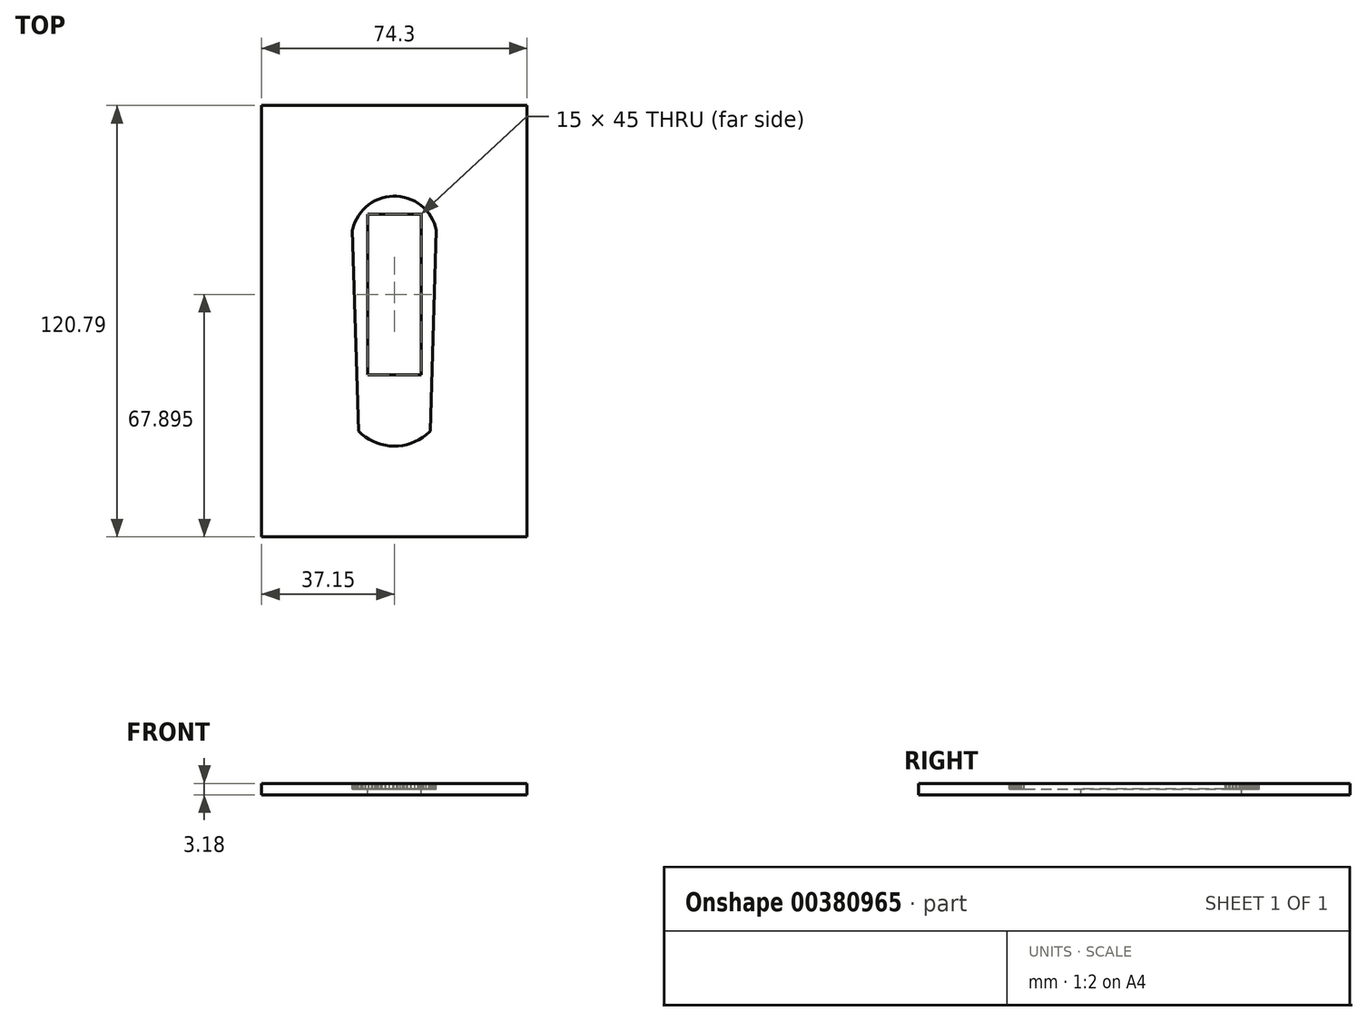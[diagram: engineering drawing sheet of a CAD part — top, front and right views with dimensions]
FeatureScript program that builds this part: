
annotation { "Feature Type Name" : "Feature", "Feature Type Description" : "" }
export const myFeature = defineFeature(function(context is Context, id is Id, definition is map)
    precondition{}
    {
        {
            var Q0;
            Q0=qCreatedBy(makeId("Top.planeOp"),FACE);
            var sketch = newSketch(context, id + "F0", { "sketchPlane" : qUnion([Q0])});
            skLineSegment(sketch, "E0", {"start": v(-11.75, 70.44) * mm, "end": v(-10, 14.2) * mm});
            skLineSegment(sketch, "E1", {"start": v(10, 14.2) * mm, "end": v(11.75, 70.44) * mm});
            skCircle(sketch, "E2", {"center": v(0, 64) * mm, "radius": 1.12 * mm, "construction": true});
            skCircle(sketch, "E3", {"center": v(0, 12.42) * mm, "radius": 1.12 * mm, "construction": true});
            skLineSegment(sketch, "E4", {"start": v(11.75, 70.44) * mm, "end": v(11.5, 71.45) * mm});
            skLineSegment(sketch, "E5", {"start": v(11.5, 71.45) * mm, "end": v(11.15, 72.44) * mm});
            skLineSegment(sketch, "E6", {"start": v(11.15, 72.44) * mm, "end": v(10.72, 73.4) * mm});
            skLineSegment(sketch, "E7", {"start": v(10.72, 73.4) * mm, "end": v(10.2, 74.3) * mm});
            skLineSegment(sketch, "E8", {"start": v(10.2, 74.3) * mm, "end": v(9.62, 75.17) * mm});
            skLineSegment(sketch, "E9", {"start": v(9.62, 75.17) * mm, "end": v(8.96, 75.99) * mm});
            skLineSegment(sketch, "E10", {"start": v(8.96, 75.99) * mm, "end": v(8.23, 76.74) * mm});
            skLineSegment(sketch, "E11", {"start": v(8.23, 76.74) * mm, "end": v(7.43, 77.42) * mm});
            skLineSegment(sketch, "E12", {"start": v(7.43, 77.42) * mm, "end": v(6.59, 78.03) * mm});
            skLineSegment(sketch, "E13", {"start": v(6.59, 78.03) * mm, "end": v(5.69, 78.57) * mm});
            skLineSegment(sketch, "E14", {"start": v(5.69, 78.57) * mm, "end": v(4.74, 79.02) * mm});
            skLineSegment(sketch, "E15", {"start": v(4.74, 79.02) * mm, "end": v(3.76, 79.4) * mm});
            skLineSegment(sketch, "E16", {"start": v(3.76, 79.4) * mm, "end": v(2.76, 79.68) * mm});
            skLineSegment(sketch, "E17", {"start": v(2.76, 79.68) * mm, "end": v(1.73, 79.87) * mm});
            skLineSegment(sketch, "E18", {"start": v(1.73, 79.87) * mm, "end": v(0.69, 79.98) * mm});
            skLineSegment(sketch, "E19", {"start": v(0.69, 79.98) * mm, "end": v(-0.36, 80) * mm});
            skLineSegment(sketch, "E20", {"start": v(-0.36, 80) * mm, "end": v(-1.4, 79.92) * mm});
            skLineSegment(sketch, "E21", {"start": v(-1.4, 79.92) * mm, "end": v(-2.44, 79.75) * mm});
            skLineSegment(sketch, "E22", {"start": v(-2.44, 79.75) * mm, "end": v(-3.45, 79.5) * mm});
            skLineSegment(sketch, "E23", {"start": v(-3.45, 79.5) * mm, "end": v(-4.44, 79.15) * mm});
            skLineSegment(sketch, "E24", {"start": v(-4.44, 79.15) * mm, "end": v(-5.4, 78.72) * mm});
            skLineSegment(sketch, "E25", {"start": v(-5.4, 78.72) * mm, "end": v(-6.3, 78.2) * mm});
            skLineSegment(sketch, "E26", {"start": v(-6.3, 78.2) * mm, "end": v(-7.17, 77.62) * mm});
            skLineSegment(sketch, "E27", {"start": v(-7.17, 77.62) * mm, "end": v(-7.99, 76.96) * mm});
            skLineSegment(sketch, "E28", {"start": v(-7.99, 76.96) * mm, "end": v(-8.74, 76.23) * mm});
            skLineSegment(sketch, "E29", {"start": v(-8.74, 76.23) * mm, "end": v(-9.42, 75.43) * mm});
            skLineSegment(sketch, "E30", {"start": v(-9.42, 75.43) * mm, "end": v(-10.03, 74.59) * mm});
            skLineSegment(sketch, "E31", {"start": v(-10.03, 74.59) * mm, "end": v(-10.57, 73.69) * mm});
            skLineSegment(sketch, "E32", {"start": v(-10.57, 73.69) * mm, "end": v(-11.02, 72.74) * mm});
            skLineSegment(sketch, "E33", {"start": v(-11.02, 72.74) * mm, "end": v(-11.4, 71.76) * mm});
            skLineSegment(sketch, "E34", {"start": v(-11.4, 71.76) * mm, "end": v(-11.68, 70.76) * mm});
            skLineSegment(sketch, "E35", {"start": v(-11.68, 70.76) * mm, "end": v(-11.75, 70.44) * mm});
            skLineSegment(sketch, "E36", {"start": v(-10, 14.2) * mm, "end": v(-9.1, 13.37) * mm});
            skLineSegment(sketch, "E37", {"start": v(-9.1, 13.37) * mm, "end": v(-8.15, 12.61) * mm});
            skLineSegment(sketch, "E38", {"start": v(-8.15, 12.61) * mm, "end": v(-7.12, 11.95) * mm});
            skLineSegment(sketch, "E39", {"start": v(-7.12, 11.95) * mm, "end": v(-6.05, 11.37) * mm});
            skLineSegment(sketch, "E40", {"start": v(-6.05, 11.37) * mm, "end": v(-4.92, 10.9) * mm});
            skLineSegment(sketch, "E41", {"start": v(-4.92, 10.9) * mm, "end": v(-3.76, 10.51) * mm});
            skLineSegment(sketch, "E42", {"start": v(-3.76, 10.51) * mm, "end": v(-2.57, 10.24) * mm});
            skLineSegment(sketch, "E43", {"start": v(-2.57, 10.24) * mm, "end": v(-1.36, 10.07) * mm});
            skLineSegment(sketch, "E44", {"start": v(-1.36, 10.07) * mm, "end": v(-0.14, 10) * mm});
            skLineSegment(sketch, "E45", {"start": v(-0.14, 10) * mm, "end": v(1.08, 10.04) * mm});
            skLineSegment(sketch, "E46", {"start": v(1.08, 10.04) * mm, "end": v(2.3, 10.19) * mm});
            skLineSegment(sketch, "E47", {"start": v(2.3, 10.19) * mm, "end": v(3.49, 10.44) * mm});
            skLineSegment(sketch, "E48", {"start": v(3.49, 10.44) * mm, "end": v(4.65, 10.8) * mm});
            skLineSegment(sketch, "E49", {"start": v(4.65, 10.8) * mm, "end": v(5.79, 11.25) * mm});
            skLineSegment(sketch, "E50", {"start": v(5.79, 11.25) * mm, "end": v(6.88, 11.8) * mm});
            skLineSegment(sketch, "E51", {"start": v(6.88, 11.8) * mm, "end": v(7.91, 12.45) * mm});
            skLineSegment(sketch, "E52", {"start": v(7.91, 12.45) * mm, "end": v(8.89, 13.18) * mm});
            skLineSegment(sketch, "E53", {"start": v(8.89, 13.18) * mm, "end": v(9.8, 14) * mm});
            skLineSegment(sketch, "E54", {"start": v(9.8, 14) * mm, "end": v(10, 14.2) * mm});
            skCircle(sketch, "E55", {"center": v(-0.85, 17.78) * mm, "radius": 0.45 * mm, "construction": true});
            skCircle(sketch, "E56", {"center": v(0.85, 17.78) * mm, "radius": 0.35 * mm, "construction": true});
            skCircle(sketch, "E57", {"center": v(2.84, 26.11) * mm, "radius": 0.5 * mm, "construction": true});
            skCircle(sketch, "E58", {"center": v(1.83, 31.2) * mm, "radius": 0.5 * mm, "construction": true});
            skCircle(sketch, "E59", {"center": v(3.86, 31.2) * mm, "radius": 0.5 * mm, "construction": true});
            skSolve(sketch);
        }
        {
            var Q0;
            Q0=qCreatedBy(makeId("Top.planeOp"),FACE);
            var sketch = newSketch(context, id + "F1", { "sketchPlane" : qUnion([Q0])});
            skLineSegment(sketch, "E60.bottom", {"start": v(-11.75, 80) * mm, "end": v(11.75, 80) * mm, "construction": true});
            skLineSegment(sketch, "E60.top", {"start": v(-11.75, 10) * mm, "end": v(11.75, 10) * mm, "construction": true});
            skLineSegment(sketch, "E60.left", {"start": v(-11.75, 80) * mm, "end": v(-11.75, 10) * mm, "construction": true});
            skLineSegment(sketch, "E60.right", {"start": v(11.75, 80) * mm, "end": v(11.75, 10) * mm, "construction": true});
            skLineSegment(sketch, "E61.0", {"start": v(-37.15, 105.4) * mm, "end": v(-37.15, -15.4) * mm});
            skLineSegment(sketch, "E61.1", {"start": v(-37.15, 105.4) * mm, "end": v(37.15, 105.4) * mm});
            skLineSegment(sketch, "E61.2", {"start": v(37.15, 105.4) * mm, "end": v(37.15, -15.4) * mm});
            skLineSegment(sketch, "E61.3", {"start": v(-37.15, -15.4) * mm, "end": v(37.15, -15.4) * mm});
            skSolve(sketch);
        }
        {
            var Q0;
            Q0 = qSketchRegion(id + "F1", true);
            extrude(context, id + "F2", {"entities" : qUnion([Q0]), "oppositeDirection" : true, "depth" : 3.17 * mm});
        }
        {
            var Q0;
            Q0 = qSketchRegion(id + "F0", true);
            extrude(context, id + "F3", {"entities" : qUnion([Q0]), "operationType" : NewBodyOperationType.REMOVE, "oppositeDirection" : true, "depth" : 1.57 * mm});
        }
        {
            var Q0;
            Q0=makeQuery(id+"F3.boolean.opBoolean","COPY",FACE,{"derivedFrom":makeQuery(id+"F3.opExtrude","CAP_FACE",FACE,{"disambiguationData":[OSD([sQuery(id+"F0.wireOp",EDGE,"E0"),sQuery(id+"F0.wireOp",EDGE,"E1"),sQuery(id+"F0.wireOp",EDGE,"E4"),sQuery(id+"F0.wireOp",EDGE,"E5"),sQuery(id+"F0.wireOp",EDGE,"E6"),sQuery(id+"F0.wireOp",EDGE,"E7"),sQuery(id+"F0.wireOp",EDGE,"E8"),sQuery(id+"F0.wireOp",EDGE,"E9"),sQuery(id+"F0.wireOp",EDGE,"E10"),sQuery(id+"F0.wireOp",EDGE,"E11"),sQuery(id+"F0.wireOp",EDGE,"E12"),sQuery(id+"F0.wireOp",EDGE,"E13"),sQuery(id+"F0.wireOp",EDGE,"E14"),sQuery(id+"F0.wireOp",EDGE,"E15"),sQuery(id+"F0.wireOp",EDGE,"E16"),sQuery(id+"F0.wireOp",EDGE,"E17"),sQuery(id+"F0.wireOp",EDGE,"E18"),sQuery(id+"F0.wireOp",EDGE,"E19"),sQuery(id+"F0.wireOp",EDGE,"E20"),sQuery(id+"F0.wireOp",EDGE,"E21"),sQuery(id+"F0.wireOp",EDGE,"E22"),sQuery(id+"F0.wireOp",EDGE,"E23"),sQuery(id+"F0.wireOp",EDGE,"E24"),sQuery(id+"F0.wireOp",EDGE,"E25"),sQuery(id+"F0.wireOp",EDGE,"E26"),sQuery(id+"F0.wireOp",EDGE,"E27"),sQuery(id+"F0.wireOp",EDGE,"E28"),sQuery(id+"F0.wireOp",EDGE,"E29"),sQuery(id+"F0.wireOp",EDGE,"E30"),sQuery(id+"F0.wireOp",EDGE,"E31"),sQuery(id+"F0.wireOp",EDGE,"E32"),sQuery(id+"F0.wireOp",EDGE,"E33"),sQuery(id+"F0.wireOp",EDGE,"E34"),sQuery(id+"F0.wireOp",EDGE,"E35"),sQuery(id+"F0.wireOp",EDGE,"E36"),sQuery(id+"F0.wireOp",EDGE,"E37"),sQuery(id+"F0.wireOp",EDGE,"E38"),sQuery(id+"F0.wireOp",EDGE,"E39"),sQuery(id+"F0.wireOp",EDGE,"E40"),sQuery(id+"F0.wireOp",EDGE,"E41"),sQuery(id+"F0.wireOp",EDGE,"E42"),sQuery(id+"F0.wireOp",EDGE,"E43"),sQuery(id+"F0.wireOp",EDGE,"E44"),sQuery(id+"F0.wireOp",EDGE,"E45"),sQuery(id+"F0.wireOp",EDGE,"E46"),sQuery(id+"F0.wireOp",EDGE,"E47"),sQuery(id+"F0.wireOp",EDGE,"E48"),sQuery(id+"F0.wireOp",EDGE,"E49"),sQuery(id+"F0.wireOp",EDGE,"E50"),sQuery(id+"F0.wireOp",EDGE,"E51"),sQuery(id+"F0.wireOp",EDGE,"E52"),sQuery(id+"F0.wireOp",EDGE,"E53"),sQuery(id+"F0.wireOp",EDGE,"E54")])],"isStart":false})});
            var sketch = newSketch(context, id + "F4", { "sketchPlane" : qUnion([Q0])});
            skLineSegment(sketch, "E62.bottom", {"start": v(-7.5, 75) * mm, "end": v(7.5, 75) * mm});
            skLineSegment(sketch, "E62.top", {"start": v(-7.5, 30) * mm, "end": v(7.5, 30) * mm});
            skLineSegment(sketch, "E62.left", {"start": v(-7.5, 75) * mm, "end": v(-7.5, 30) * mm});
            skLineSegment(sketch, "E62.right", {"start": v(7.5, 75) * mm, "end": v(7.5, 30) * mm});
            skLineSegment(sketch, "E63", {"start": v(0, 30) * mm, "end": v(0, 0) * mm});
            skSolve(sketch);
        }
        {
            var Q0;
            Q0 = qSketchRegion(id + "F4", true);
            extrude(context, id + "F5", {"entities" : qUnion([Q0]), "operationType" : NewBodyOperationType.REMOVE, "endBound" : BoundingType.THROUGH_ALL, "oppositeDirection" : true, "depth" : 25.4 * mm});
        }
        {
            var Q0;
            Q0=qCreatedBy(makeId("Top.planeOp"),FACE);
            var sketch = newSketch(context, id + "F6", { "sketchPlane" : qUnion([Q0])});
            skLineSegment(sketch, "E64.0", {"start": v(-11.26, 72.84) * mm, "end": v(-11.64, 71.84) * mm});
            skLineSegment(sketch, "E64.1", {"start": v(-10.8, 73.8) * mm, "end": v(-11.26, 72.84) * mm});
            skLineSegment(sketch, "E64.2", {"start": v(-10.24, 74.73) * mm, "end": v(-10.8, 73.8) * mm});
            skLineSegment(sketch, "E64.3", {"start": v(-9.62, 75.6) * mm, "end": v(-10.24, 74.73) * mm});
            skLineSegment(sketch, "E64.4", {"start": v(-8.92, 76.4) * mm, "end": v(-9.62, 75.6) * mm});
            skLineSegment(sketch, "E64.5", {"start": v(-8.15, 77.15) * mm, "end": v(-8.92, 76.4) * mm});
            skLineSegment(sketch, "E64.6", {"start": v(-7.33, 77.82) * mm, "end": v(-8.15, 77.15) * mm});
            skLineSegment(sketch, "E64.7", {"start": v(9.97, 13.82) * mm, "end": v(10.25, 14.1) * mm});
            skLineSegment(sketch, "E64.8", {"start": v(9.05, 12.99) * mm, "end": v(9.97, 13.82) * mm});
            skLineSegment(sketch, "E64.9", {"start": v(8.06, 12.24) * mm, "end": v(9.05, 12.99) * mm});
            skLineSegment(sketch, "E64.10", {"start": v(7, 11.58) * mm, "end": v(8.06, 12.24) * mm});
            skLineSegment(sketch, "E64.11", {"start": v(5.9, 11.02) * mm, "end": v(7, 11.58) * mm});
            skLineSegment(sketch, "E64.12", {"start": v(4.74, 10.56) * mm, "end": v(5.9, 11.02) * mm});
            skLineSegment(sketch, "E64.13", {"start": v(3.55, 10.2) * mm, "end": v(4.74, 10.56) * mm});
            skLineSegment(sketch, "E64.14", {"start": v(2.33, 9.94) * mm, "end": v(3.55, 10.2) * mm});
            skLineSegment(sketch, "E64.15", {"start": v(1.1, 9.79) * mm, "end": v(2.33, 9.94) * mm});
            skLineSegment(sketch, "E64.16", {"start": v(-0.15, 9.75) * mm, "end": v(1.1, 9.79) * mm});
            skLineSegment(sketch, "E64.17", {"start": v(-1.39, 9.81) * mm, "end": v(-0.15, 9.75) * mm});
            skLineSegment(sketch, "E64.18", {"start": v(-2.62, 9.99) * mm, "end": v(-1.39, 9.81) * mm});
            skLineSegment(sketch, "E64.19", {"start": v(-10.25, 14.09) * mm, "end": v(-9.27, 13.17) * mm});
            skLineSegment(sketch, "E64.20", {"start": v(-12, 70.46) * mm, "end": v(-10.25, 14.09) * mm});
            skLineSegment(sketch, "E64.21", {"start": v(-11.93, 70.82) * mm, "end": v(-12, 70.46) * mm});
            skLineSegment(sketch, "E64.22", {"start": v(-11.64, 71.84) * mm, "end": v(-11.93, 70.82) * mm});
            skLineSegment(sketch, "E64.23", {"start": v(-9.27, 13.17) * mm, "end": v(-8.3, 12.4) * mm});
            skLineSegment(sketch, "E64.24", {"start": v(-8.3, 12.4) * mm, "end": v(-7.25, 11.73) * mm});
            skLineSegment(sketch, "E64.25", {"start": v(-7.25, 11.73) * mm, "end": v(-6.16, 11.14) * mm});
            skLineSegment(sketch, "E64.26", {"start": v(-6.16, 11.14) * mm, "end": v(-5.01, 10.66) * mm});
            skLineSegment(sketch, "E64.27", {"start": v(-5.01, 10.66) * mm, "end": v(-3.83, 10.27) * mm});
            skLineSegment(sketch, "E64.28", {"start": v(-3.83, 10.27) * mm, "end": v(-2.62, 9.99) * mm});
            skLineSegment(sketch, "E64.29", {"start": v(10.25, 14.1) * mm, "end": v(12, 70.46) * mm});
            skLineSegment(sketch, "E64.30", {"start": v(12, 70.46) * mm, "end": v(11.74, 71.52) * mm});
            skLineSegment(sketch, "E64.31", {"start": v(11.74, 71.52) * mm, "end": v(11.38, 72.53) * mm});
            skLineSegment(sketch, "E64.32", {"start": v(11.38, 72.53) * mm, "end": v(10.95, 73.5) * mm});
            skLineSegment(sketch, "E64.33", {"start": v(10.95, 73.5) * mm, "end": v(10.42, 74.44) * mm});
            skLineSegment(sketch, "E64.34", {"start": v(10.42, 74.44) * mm, "end": v(9.82, 75.33) * mm});
            skLineSegment(sketch, "E64.35", {"start": v(9.82, 75.33) * mm, "end": v(9.15, 76.15) * mm});
            skLineSegment(sketch, "E64.36", {"start": v(9.15, 76.15) * mm, "end": v(8.4, 76.92) * mm});
            skLineSegment(sketch, "E64.37", {"start": v(8.4, 76.92) * mm, "end": v(7.6, 77.62) * mm});
            skLineSegment(sketch, "E64.38", {"start": v(7.6, 77.62) * mm, "end": v(6.73, 78.24) * mm});
            skLineSegment(sketch, "E64.39", {"start": v(6.73, 78.24) * mm, "end": v(5.8, 78.8) * mm});
            skLineSegment(sketch, "E64.40", {"start": v(5.8, 78.8) * mm, "end": v(4.84, 79.26) * mm});
            skLineSegment(sketch, "E64.41", {"start": v(4.84, 79.26) * mm, "end": v(3.84, 79.64) * mm});
            skLineSegment(sketch, "E64.42", {"start": v(3.84, 79.64) * mm, "end": v(2.82, 79.93) * mm});
            skLineSegment(sketch, "E64.43", {"start": v(2.82, 79.93) * mm, "end": v(1.77, 80.13) * mm});
            skLineSegment(sketch, "E64.44", {"start": v(1.77, 80.13) * mm, "end": v(0.7, 80.23) * mm});
            skLineSegment(sketch, "E64.45", {"start": v(0.7, 80.23) * mm, "end": v(-0.37, 80.25) * mm});
            skLineSegment(sketch, "E64.46", {"start": v(-0.37, 80.25) * mm, "end": v(-1.43, 80.17) * mm});
            skLineSegment(sketch, "E64.47", {"start": v(-1.43, 80.17) * mm, "end": v(-2.49, 80) * mm});
            skLineSegment(sketch, "E64.48", {"start": v(-2.49, 80) * mm, "end": v(-3.52, 79.74) * mm});
            skLineSegment(sketch, "E64.49", {"start": v(-3.52, 79.74) * mm, "end": v(-4.53, 79.38) * mm});
            skLineSegment(sketch, "E64.50", {"start": v(-4.53, 79.38) * mm, "end": v(-5.5, 78.95) * mm});
            skLineSegment(sketch, "E64.51", {"start": v(-5.5, 78.95) * mm, "end": v(-6.44, 78.42) * mm});
            skLineSegment(sketch, "E64.52", {"start": v(-6.44, 78.42) * mm, "end": v(-7.33, 77.82) * mm});
            skSolve(sketch);
        }
        {
            var Q0;
            Q0 = qSketchRegion(id + "F6", true);
            var Q1;
            Q1=makeQuery(id+"F3.boolean.opBoolean","COPY",FACE,{"derivedFrom":makeQuery(id+"F3.opExtrude","CAP_FACE",FACE,{"disambiguationData":[OSD([sQuery(id+"F0.wireOp",EDGE,"E0"),sQuery(id+"F0.wireOp",EDGE,"E1"),sQuery(id+"F0.wireOp",EDGE,"E4"),sQuery(id+"F0.wireOp",EDGE,"E5"),sQuery(id+"F0.wireOp",EDGE,"E6"),sQuery(id+"F0.wireOp",EDGE,"E7"),sQuery(id+"F0.wireOp",EDGE,"E8"),sQuery(id+"F0.wireOp",EDGE,"E9"),sQuery(id+"F0.wireOp",EDGE,"E10"),sQuery(id+"F0.wireOp",EDGE,"E11"),sQuery(id+"F0.wireOp",EDGE,"E12"),sQuery(id+"F0.wireOp",EDGE,"E13"),sQuery(id+"F0.wireOp",EDGE,"E14"),sQuery(id+"F0.wireOp",EDGE,"E15"),sQuery(id+"F0.wireOp",EDGE,"E16"),sQuery(id+"F0.wireOp",EDGE,"E17"),sQuery(id+"F0.wireOp",EDGE,"E18"),sQuery(id+"F0.wireOp",EDGE,"E19"),sQuery(id+"F0.wireOp",EDGE,"E20"),sQuery(id+"F0.wireOp",EDGE,"E21"),sQuery(id+"F0.wireOp",EDGE,"E22"),sQuery(id+"F0.wireOp",EDGE,"E23"),sQuery(id+"F0.wireOp",EDGE,"E24"),sQuery(id+"F0.wireOp",EDGE,"E25"),sQuery(id+"F0.wireOp",EDGE,"E26"),sQuery(id+"F0.wireOp",EDGE,"E27"),sQuery(id+"F0.wireOp",EDGE,"E28"),sQuery(id+"F0.wireOp",EDGE,"E29"),sQuery(id+"F0.wireOp",EDGE,"E30"),sQuery(id+"F0.wireOp",EDGE,"E31"),sQuery(id+"F0.wireOp",EDGE,"E32"),sQuery(id+"F0.wireOp",EDGE,"E33"),sQuery(id+"F0.wireOp",EDGE,"E34"),sQuery(id+"F0.wireOp",EDGE,"E35"),sQuery(id+"F0.wireOp",EDGE,"E36"),sQuery(id+"F0.wireOp",EDGE,"E37"),sQuery(id+"F0.wireOp",EDGE,"E38"),sQuery(id+"F0.wireOp",EDGE,"E39"),sQuery(id+"F0.wireOp",EDGE,"E40"),sQuery(id+"F0.wireOp",EDGE,"E41"),sQuery(id+"F0.wireOp",EDGE,"E42"),sQuery(id+"F0.wireOp",EDGE,"E43"),sQuery(id+"F0.wireOp",EDGE,"E44"),sQuery(id+"F0.wireOp",EDGE,"E45"),sQuery(id+"F0.wireOp",EDGE,"E46"),sQuery(id+"F0.wireOp",EDGE,"E47"),sQuery(id+"F0.wireOp",EDGE,"E48"),sQuery(id+"F0.wireOp",EDGE,"E49"),sQuery(id+"F0.wireOp",EDGE,"E50"),sQuery(id+"F0.wireOp",EDGE,"E51"),sQuery(id+"F0.wireOp",EDGE,"E52"),sQuery(id+"F0.wireOp",EDGE,"E53"),sQuery(id+"F0.wireOp",EDGE,"E54")])],"isStart":false})});
            extrude(context, id + "F7", {"entities" : qUnion([Q0]), "operationType" : NewBodyOperationType.REMOVE, "endBound" : BoundingType.THROUGH_ALL, "endBoundEntityFace" : qUnion([Q1]), "depth" : 25.4 * mm});
        }
    });
